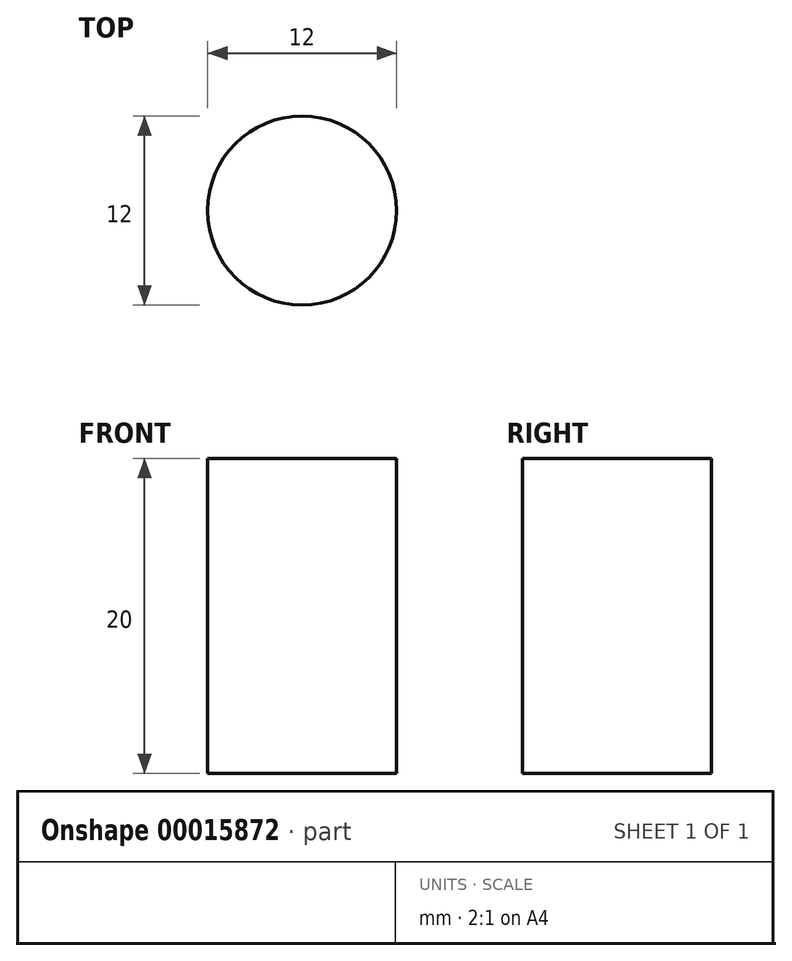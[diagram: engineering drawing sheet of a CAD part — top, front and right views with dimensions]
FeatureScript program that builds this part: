
annotation { "Feature Type Name" : "Feature", "Feature Type Description" : "" }
export const myFeature = defineFeature(function(context is Context, id is Id, definition is map)
    precondition{}
    {
        {
            var Q0;
            Q0=qCreatedBy(makeId("Top.planeOp"),FACE);
            var sketch = newSketch(context, id + "F0", { "sketchPlane" : qUnion([Q0])});
            skCircle(sketch, "E0", {"center": v(0, 0) * mm, "radius": 6 * mm});
            skSolve(sketch);
        }
        {
            var Q0;
            Q0=qSketchRegion(id+"F0",true);
            extrude(context, id + "F1", {"entities" : qUnion([Q0]), "depth" : 20 * mm});
        }
    });
